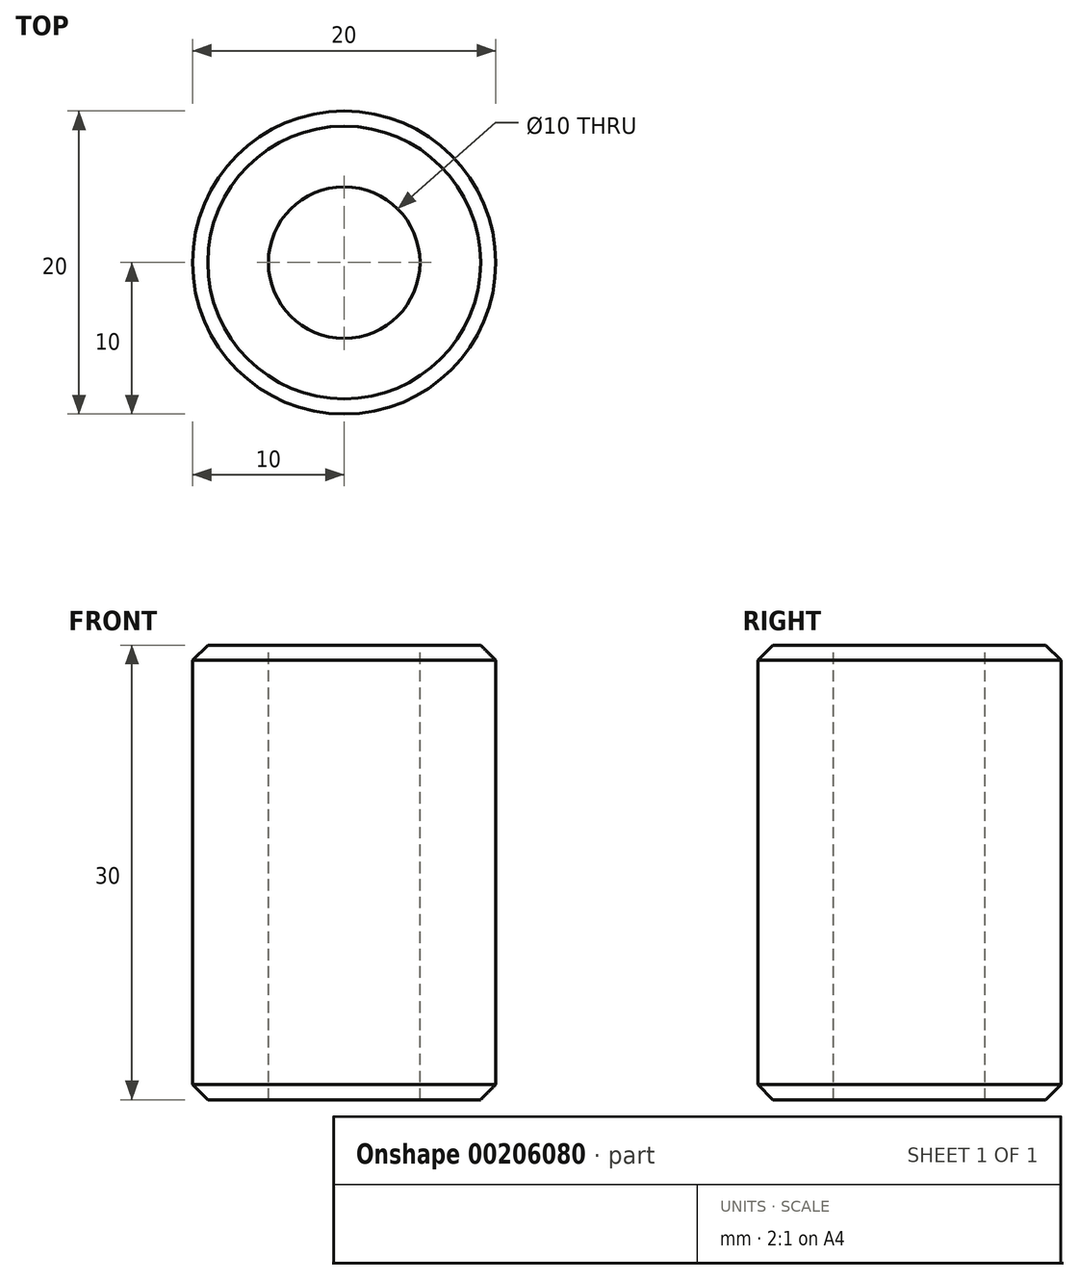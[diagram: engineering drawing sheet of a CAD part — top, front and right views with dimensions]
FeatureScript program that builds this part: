
annotation { "Feature Type Name" : "Feature", "Feature Type Description" : "" }
export const myFeature = defineFeature(function(context is Context, id is Id, definition is map)
    precondition{}
    {
        {
            var Q0;
            Q0=qCreatedBy(makeId("Top.planeOp"),FACE);
            var sketch = newSketch(context, id + "F0", { "sketchPlane" : qUnion([Q0])});
            skCircle(sketch, "E0", {"center": v(0, 0) * mm, "radius": 10 * mm});
            skSolve(sketch);
        }
        {
            var Q0;
            Q0 = qSketchRegion(id + "F0", true);
            extrude(context, id + "F1", {"entities" : qUnion([Q0]), "depth" : 30 * mm});
        }
        {
            var Q0;
            Q0=qCreatedBy(makeId("Top.planeOp"),FACE);
            var sketch = newSketch(context, id + "F2", { "sketchPlane" : qUnion([Q0])});
            skPoint(sketch, "E1", {"position": v(0, 0) * mm});
            skSolve(sketch);
        }
        {
            var Q0;
            Q0=sQuery(id+"F2.wireOp",VERTEX,"E1");
            var Q1;
            Q1=makeQuery(id+"F1.opExtrude","SWEPT_BODY",BODY,{"disambiguationData":[OSD([sQuery(id+"F0.wireOp",EDGE,"E0")])]});
            hole(context, id + "F3", {"style" : HoleStyle.SIMPLE, "endStyle" : HoleEndStyle.THROUGH, "oppositeDirection" : true, "holeDiameter" : 10 * mm, "locations" : qUnion([Q0]), "scope" : qUnion([Q1]), "isTappedThrough" : true});
        }
        {
            var Q0;
            Q0=makeQuery(id+"F1.opExtrude","SWEPT_FACE",FACE,{"disambiguationData":[OSD([sQuery(id+"F0.wireOp",EDGE,"E0")])]});
            var Q1;
            Q1=makeQuery(id+"F3.hole-0.boolean.opBoolean","COPY",FACE,{"derivedFrom":makeQuery(id+"F3.hole-0.opRevolve","SWEPT_FACE",FACE,{"disambiguationData":[OSD([sQuery(id+"F3.hole-0.sketch.wireOp",EDGE,"core_line_2")])]})});
            chamfer(context, id + "F4", {"entities" : qUnion([Q0, Q1]), "width" : 1 * mm, "tangentPropagation" : true});
        }
    });
